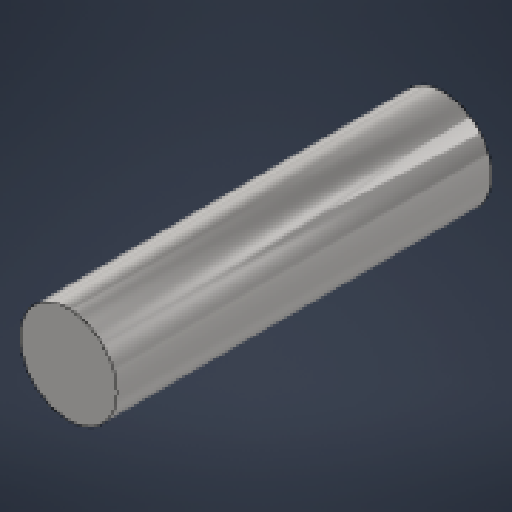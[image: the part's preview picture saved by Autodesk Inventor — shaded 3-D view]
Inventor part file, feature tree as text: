
AUTODESK INVENTOR PART (.ipt)
format: ipt  version: 2025.3 (Build 293356000, 356)  size: 173,056 bytes
history: native  units: mm
features: extrude x1, sketch x1
ambient origin geometry x8: Origin, YZ Plane, XZ Plane, XY Plane, X Axis, Y Axis, Z Axis, Center Point
bodies: Solid1 (feature_tree)
feature tree (2):
  extrude  "Extrusion1"  Depth=11.619mm TaperAngle=0.0deg
  sketch  "Sketch1"  dims[d0=3.0mm d1=11.619mm d2=0.0mm]
